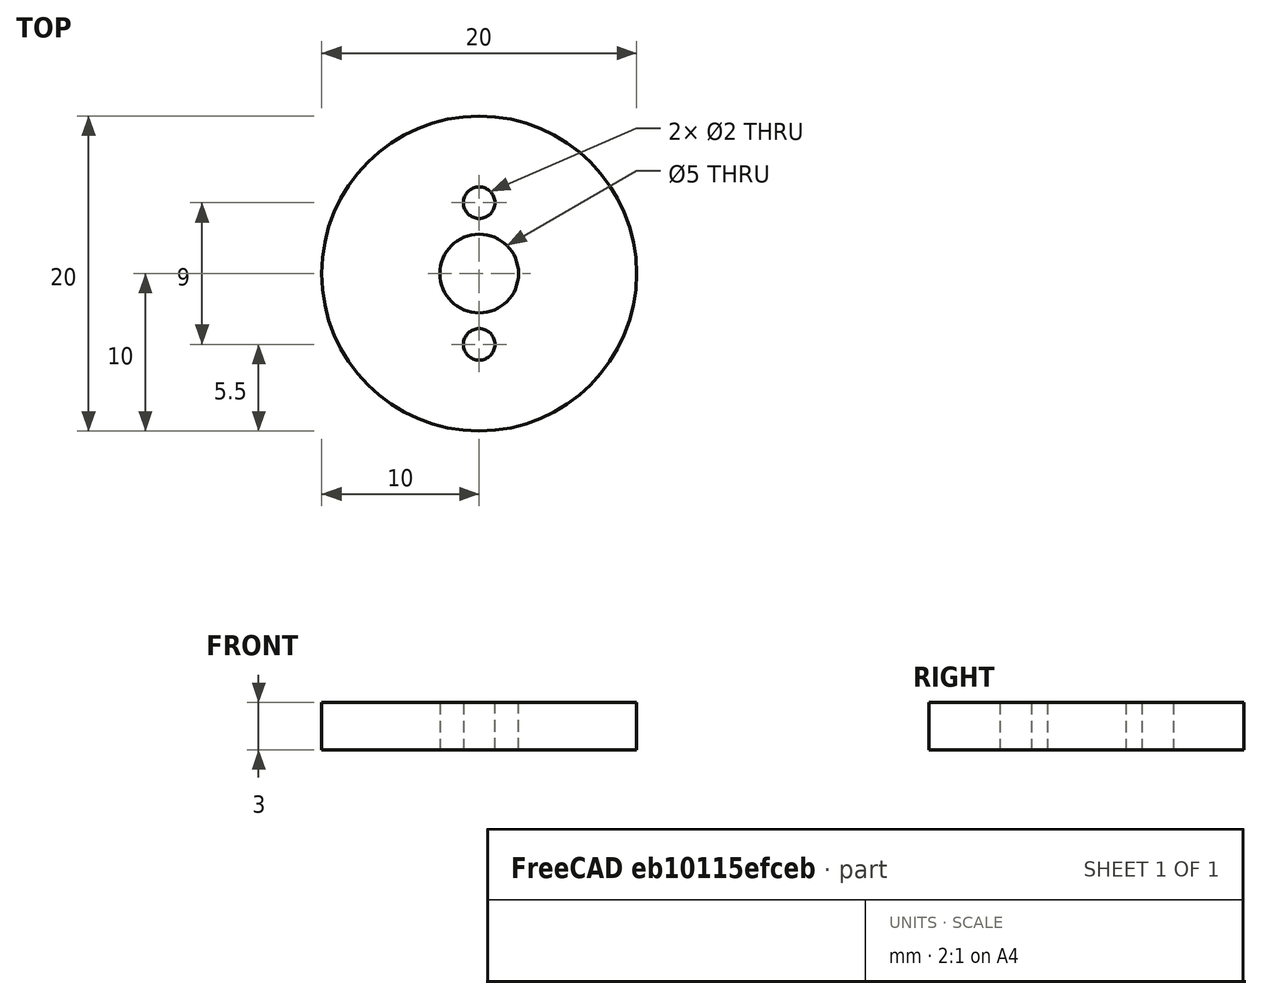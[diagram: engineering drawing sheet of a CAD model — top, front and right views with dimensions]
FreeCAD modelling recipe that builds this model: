
FCSTD DOCUMENT  (FreeCAD 0.16R6707 (Git))
Label: couplage roue 2
License: All rights reserved
LicenseURL: http://en.wikipedia.org/wiki/All_rights_reserved
objects: Sketcher::SketchObject×1, PartDesign::Pad×1
note: 3 computed .brp shape members not serialized (recipe doc carries the construction recipe); baked Part::Feature solids carry a one-line shape summary decoded from their .brp

FEATURE [Sketcher::SketchObject] Sketch
  sketch-geometry (6):
    g0: Circle CenterX=0 CenterY=0 CenterZ=0 NormalX=0 NormalY=0 NormalZ=1 Radius=10
    g1: GeomPoint [constr] X=0 Y=4.5 Z=0
    g2: GeomPoint [constr] X=0 Y=-4.5 Z=0
    g3: Circle CenterX=0 CenterY=4.5 CenterZ=0 NormalX=0 NormalY=0 NormalZ=1 Radius=1
    g4: Circle CenterX=0 CenterY=-4.5 CenterZ=0 NormalX=0 NormalY=0 NormalZ=1 Radius=1
    g5: Circle CenterX=0 CenterY=0 CenterZ=0 NormalX=0 NormalY=0 NormalZ=1 Radius=2.5
  constraints (12):
    c: Coincident(g0,g-1)
    c: Radius(g0) = 10
    c: PointOnObject(g1,g-2)
    c: PointOnObject(g2,g-2)
    c: DistanceY(g1) = 4.5
    c: DistanceY(g2) = -4.5
    c: Coincident(g3,g1)
    c: Radius(g3) = 1
    c: Coincident(g4,g2)
    c: Radius(g4) = 1
    c: Coincident(g5,g-1)
    c: Radius(g5) = 2.5
FEATURE [PartDesign::Pad] Pad
  Length = 3
  Length2 = 100
  Sketch = -> Sketch
  Type = 0
